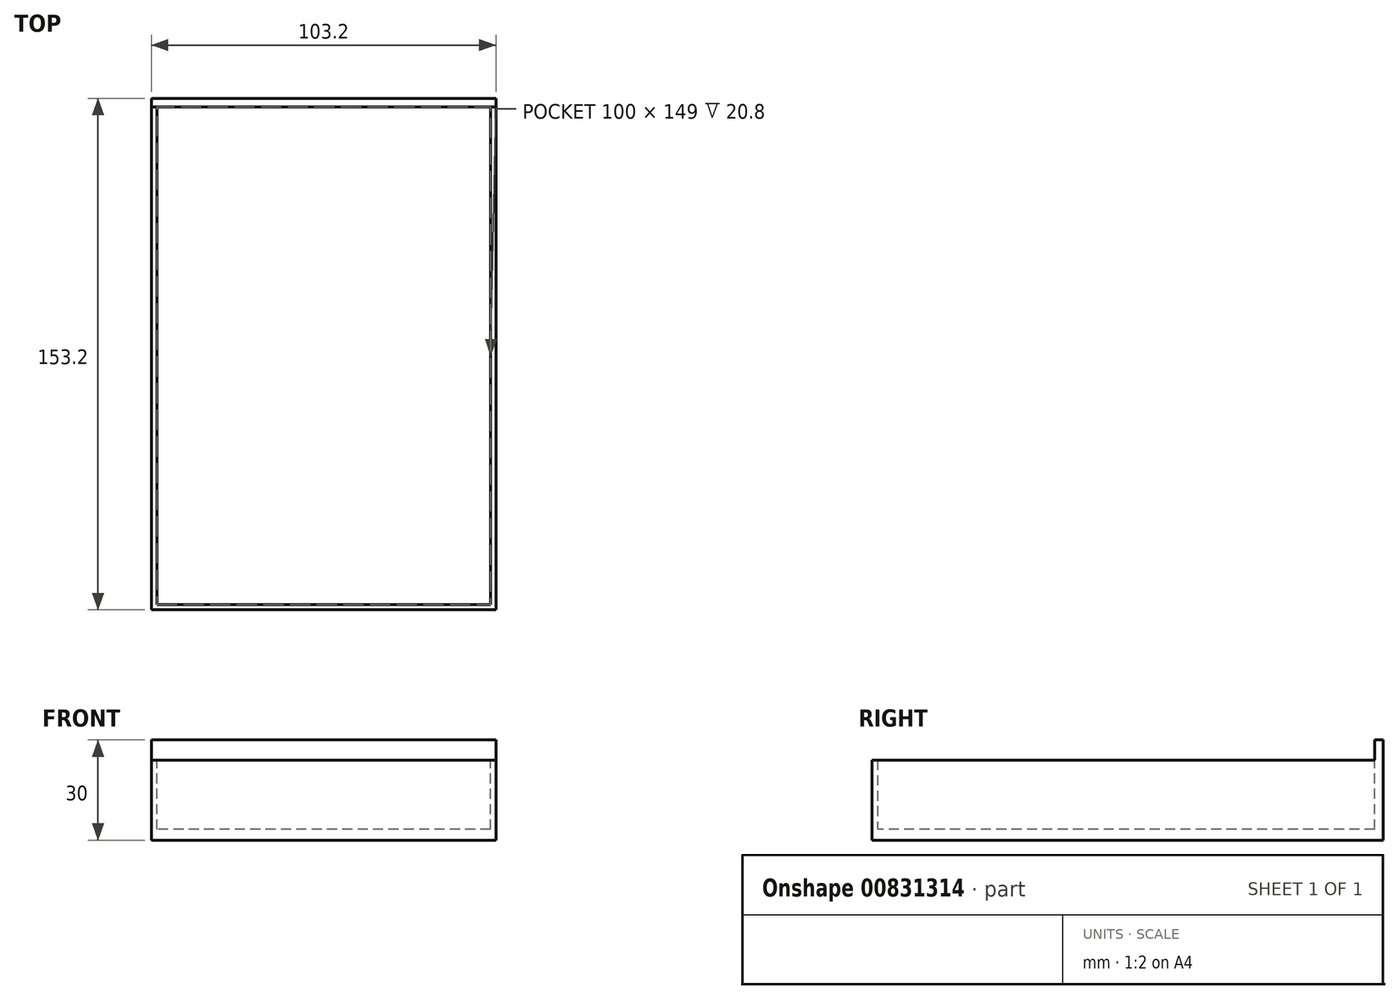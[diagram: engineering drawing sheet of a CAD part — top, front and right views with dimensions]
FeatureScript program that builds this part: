
annotation { "Feature Type Name" : "Feature", "Feature Type Description" : "" }
export const myFeature = defineFeature(function(context is Context, id is Id, definition is map)
    precondition{}
    {
        {
            var Q0;
            Q0=qCreatedBy(makeId("Top.planeOp"),FACE);
            var sketch = newSketch(context, id + "F0", { "sketchPlane" : qUnion([Q0])});
            skLineSegment(sketch, "E0.bottom", {"start": v(-51.6, 76.6) * mm, "end": v(51.6, 76.6) * mm});
            skLineSegment(sketch, "E0.top", {"start": v(-51.6, -76.6) * mm, "end": v(51.6, -76.6) * mm});
            skLineSegment(sketch, "E0.left", {"start": v(-51.6, 76.6) * mm, "end": v(-51.6, -76.6) * mm});
            skLineSegment(sketch, "E0.right", {"start": v(51.6, 76.6) * mm, "end": v(51.6, -76.6) * mm});
            skPoint(sketch, "E0.middle", {"position": v(0, 0) * mm});
            skLineSegment(sketch, "E1.bottom", {"start": v(-50, 75) * mm, "end": v(50, 75) * mm});
            skLineSegment(sketch, "E1.top", {"start": v(-50, -75) * mm, "end": v(50, -75) * mm});
            skLineSegment(sketch, "E1.left", {"start": v(-50, 75) * mm, "end": v(-50, -75) * mm});
            skLineSegment(sketch, "E1.right", {"start": v(50, 75) * mm, "end": v(50, -75) * mm});
            skSolve(sketch);
        }
        {
            var Q0;
            Q0=makeQuery(id+"F0.imprint","IMPRINT",FACE,{"disambiguationData":[TD([[makeQuery(id+"F0.imprint","IMPRINT",EDGE,{"derivedFrom":sQuery(id+"F0.wireOp",EDGE,"E0.bottom")}),-1.0]])]});
            extrude(context, id + "F1", {"entities" : qUnion([Q0]), "depth" : 24 * mm, "offsetDistance" : 25 * mm});
        }
        {
            var Q0;
            Q0=qCreatedBy(makeId("Top.planeOp"),FACE);
            var sketch = newSketch(context, id + "F2", { "sketchPlane" : qUnion([Q0])});
            skLineSegment(sketch, "E2.bottom", {"start": v(-50, 75) * mm, "end": v(50, 75) * mm});
            skLineSegment(sketch, "E2.top", {"start": v(-50, -75) * mm, "end": v(50, -75) * mm});
            skLineSegment(sketch, "E2.left", {"start": v(-50, 75) * mm, "end": v(-50, -75) * mm});
            skLineSegment(sketch, "E2.right", {"start": v(50, 75) * mm, "end": v(50, -75) * mm});
            skPoint(sketch, "E2.middle", {"position": v(0, 0) * mm});
            skSolve(sketch);
        }
        {
            var Q0;
            Q0=makeQuery(id+"F2.imprint","IMPRINT",FACE,{"disambiguationData":[TD([[makeQuery(id+"F2.imprint","IMPRINT",EDGE,{"derivedFrom":sQuery(id+"F2.wireOp",EDGE,"E2.bottom")}),-1.0]])]});
            extrude(context, id + "F3", {"entities" : qUnion([Q0]), "operationType" : NewBodyOperationType.ADD, "depth" : 3.2 * mm, "offsetDistance" : 25 * mm});
        }
        {
            var Q0;
            Q0=qCreatedBy(makeId("Top.planeOp"),FACE);
            var sketch = newSketch(context, id + "F4", { "sketchPlane" : qUnion([Q0])});
            skLineSegment(sketch, "E3.bottom", {"start": v(-51.6, 76.6) * mm, "end": v(51.6, 76.6) * mm});
            skLineSegment(sketch, "E3.top", {"start": v(-51.6, 74) * mm, "end": v(51.6, 74) * mm});
            skLineSegment(sketch, "E3.left", {"start": v(-51.6, 76.6) * mm, "end": v(-51.6, 74) * mm});
            skLineSegment(sketch, "E3.right", {"start": v(51.6, 76.6) * mm, "end": v(51.6, 74) * mm});
            skPoint(sketch, "E3.middle", {"position": v(0, 75.3) * mm});
            skSolve(sketch);
        }
        {
            var Q0;
            Q0=makeQuery(id+"F4.imprint","IMPRINT",FACE,{"disambiguationData":[TD([[makeQuery(id+"F4.imprint","IMPRINT",EDGE,{"derivedFrom":sQuery(id+"F4.wireOp",EDGE,"E3.bottom")}),-1.0]])]});
            extrude(context, id + "F5", {"entities" : qUnion([Q0]), "operationType" : NewBodyOperationType.ADD, "depth" : 30 * mm, "offsetDistance" : 25 * mm});
        }
    });
